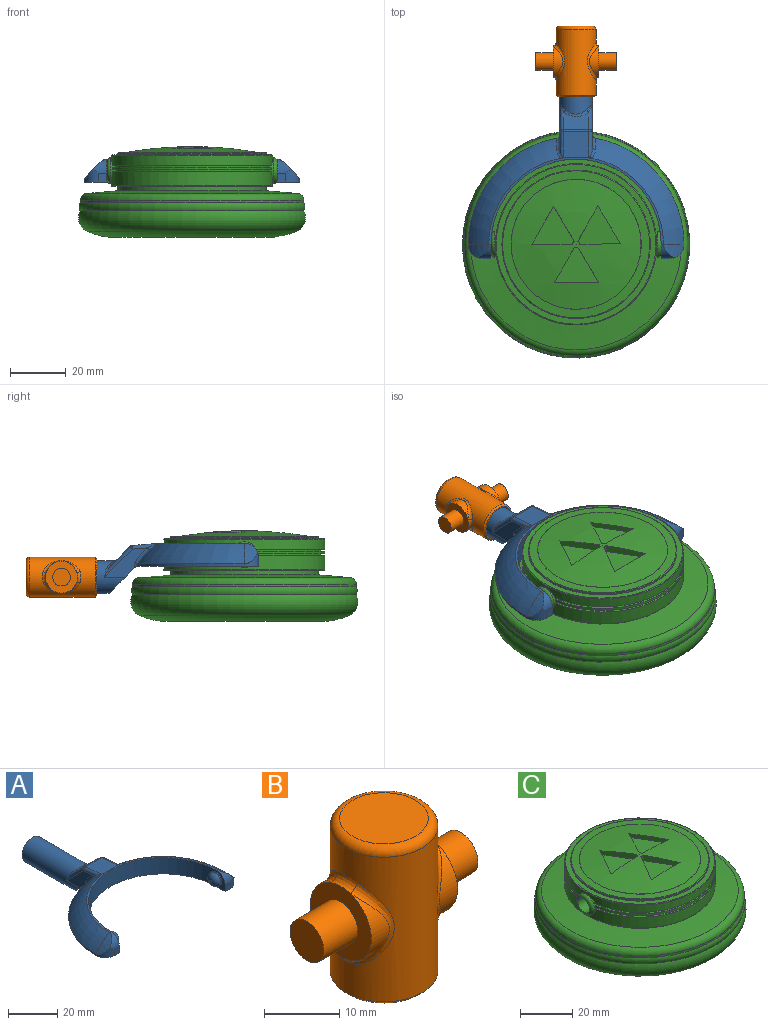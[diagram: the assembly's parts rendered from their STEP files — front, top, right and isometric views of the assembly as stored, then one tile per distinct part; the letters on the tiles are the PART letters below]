
ASSEMBLY  parts=3 mates=2
PART A: 48 faces, bbox 77.3x80.8x18.2 mm
  f0: plane 11.99x9.83mm, normal (0,-0.71,-0.71), area 141.5mm2, adj f1,f2,f9,f30,f43,f46
  f1: plane 15.39x10.49mm, normal (-1,0,0), area 63.5mm2, adj f0,f30,f32,f36,f46,f47
  f2: plane 15.39x10.49mm, normal (1,0,0), area 63.5mm2, adj f0,f30,f34,f39,f43,f44
  f3: plane 9.14x6.37mm, normal (0,0.71,0.71), area 67.6mm2, adj f35,f36,f39,f40
  f4: cylinder r=38.61mm len=37.99mm, axis (0,0,-1), area 42.6mm2, adj f6,f9,f17,f46,f47
  f5: torus R=19.3mm, axis (0,0,-1), area 507.8mm2, adj f10,f11,f12,f29,f42,f44
  f6: torus R=19.3mm, axis (0,0,-1), area 507.8mm2, adj f4,f11,f15,f28,f45,f47
  f7: cylinder r=30.48mm len=60.96mm, axis (0,0,-1), area 746.6mm2, adj f8,f9,f11,f14,f21,f24
  f8: plane 8.13x5.08mm, normal (-1,0,0), area 19.9mm2, adj f7,f9,f13,f19,f24
  f9: plane 77.22x43.73mm, normal (0,0,-1), area 956.2mm2, adj f0,f4,f7,f8,f10,f13,f14,f16
  f10: cylinder r=38.61mm len=37.99mm, axis (0,0,-1), area 42.6mm2, adj f5,f9,f20,f43,f44
  f11: plane 62.55x30.95mm, normal (0,0,1), area 75mm2, adj f5,f6,f7,f18,f19,f27
  f12: cylinder r=22.71mm len=7.33mm, axis (0,1,0), area 24.8mm2, adj f5,f19,f20
  f13: plane 3.05x3.05mm, normal (0,-1,0), area 9.3mm2, adj f8,f9,f19,f20
  f14: plane 8.13x5.08mm, normal (1,0,0), area 19.9mm2, adj f7,f9,f16,f18,f21
  f15: cylinder r=22.71mm len=7.33mm, axis (0,1,0), area 24.8mm2, adj f6,f17,f18
  f16: plane 3.05x3.05mm, normal (0,-1,0), area 9.3mm2, adj f9,f14,f17,f18
  f17: cylinder r=5.08mm len=5.08mm, axis (0,0,-1), area 21.9mm2, adj f4,f9,f15,f16,f18
  f18: cylinder r=5.08mm len=5.08mm, axis (-1,0,0), area 21.9mm2, adj f11,f14,f15,f16,f17
  f19: cylinder r=5.08mm len=5.08mm, axis (-1,0,0), area 21.9mm2, adj f8,f11,f12,f13,f20
  f20: cylinder r=5.08mm len=5.08mm, axis (0,0,-1), area 21.9mm2, adj f9,f10,f12,f13,f19
  f21: cylinder r=3.17mm len=6.35mm, axis (-1,0,0), area 12.7mm2, adj f7,f14,f23
  f22: plane 1.27x1.27mm, normal (1,0,0), area 1.3mm2, adj f23
  f23: torus R=0.64mm, axis (1,0,0), area 56.5mm2, adj f21,f22
  f24: cylinder r=3.17mm len=6.35mm, axis (1,0,0), area 12.7mm2, adj f7,f8,f26
  f25: plane 1.27x1.27mm, normal (-1,0,0), area 1.3mm2, adj f26
  f26: torus R=0.64mm, axis (-1,0,0), area 56.5mm2, adj f24,f25
  f27: plane 9.86x9.36mm, normal (0,0.09,1), area 85.6mm2, adj f11,f28,f29,f32,f34,f35,f42,f45
  f28: plane 1.04x0.17mm, normal (0,-1,0), area 0mm2, adj f6,f27,f45
  f29: plane 1.04x0.17mm, normal (0,-1,0), area 0mm2, adj f5,f27,f42
  f30: cylinder r=5.84mm len=33.01mm, axis (0,-1,0), area 1029.7mm2, adj f0,f1,f2,f31,f38,f40,f41
  f31: plane 11.68x11.68mm, normal (0,1,0), area 107.2mm2, adj f30
  f32: cylinder r=1.27mm len=9.13mm, axis (0,-1,0.09), area 14.4mm2, adj f1,f27,f33,f45
  f33: sphere r=1.27mm, area 1.5mm2, adj f32,f35,f36
  f34: cylinder r=1.27mm len=9.13mm, axis (0,1,-0.09), area 14.4mm2, adj f2,f27,f37,f42
  f35: cylinder r=1.27mm len=9.14mm, axis (-1,0,0), area 8.1mm2, adj f3,f27,f33,f37
  f36: cylinder r=1.27mm len=10.91mm, axis (0,-0.71,0.71), area 23.1mm2, adj f1,f3,f33,f38
  f37: sphere r=1.27mm, area 1.5mm2, adj f34,f35,f39
  f38: bspline ~4.55x2.75mm, area 2.3mm2, adj f30,f36,f40
  f39: cylinder r=1.27mm len=10.91mm, axis (0,0.71,-0.71), area 23.1mm2, adj f2,f3,f37,f41
  f40: bspline ~9.14x2.56mm, area 10.7mm2, adj f3,f30,f38,f41
  f41: bspline ~5.23x3.53mm, area 2.3mm2, adj f30,f39,f40
  f42: bspline ~4.62x3.14mm, area 5.2mm2, adj f5,f27,f29,f34,f44
  f43: cylinder r=1.27mm len=1.74mm, axis (0,0,-1), area 1.9mm2, adj f0,f2,f9,f10,f44
  f44: bspline ~8.6x7.86mm, area 11.9mm2, adj f2,f5,f10,f42,f43
  f45: bspline ~4.62x3.14mm, area 5.2mm2, adj f6,f27,f28,f32,f47
  f46: cylinder r=1.27mm len=1.74mm, axis (0,0,-1), area 1.9mm2, adj f0,f1,f4,f9,f47
  f47: bspline ~8.6x7.86mm, area 11.9mm2, adj f1,f4,f6,f45,f46
PART B: 25 faces, bbox 28.9x15.5x25.4 mm
  f0: cylinder r=5.71mm len=10.81mm, axis (-1,0,0), area 26.2mm2, adj f5,f15
  f1: cylinder r=5.71mm len=10.81mm, axis (-1,0,0), area 26.2mm2, adj f8,f11
  f2: cylinder r=7.14mm len=23.5mm, axis (0,0,-1), area 763.2mm2, adj f9,f10,f11,f12,f13,f14,f15,f16
  f3: plane 11.75x11.75mm, normal (0,0,1), area 108.4mm2, adj f17
  f4: plane 13.02x13.02mm, normal (0,0,-1), area 16.3mm2, adj f22,f24
  f5: plane 11.46x11.46mm, normal (1,0,0), area 70.9mm2, adj f0,f6,f13,f16,f18
  f6: cylinder r=5.71mm len=10.81mm, axis (-1,0,0), area 26.2mm2, adj f5,f14
  f7: cylinder r=5.71mm len=10.81mm, axis (-1,0,0), area 26.2mm2, adj f8,f10
  f8: plane 11.46x11.46mm, normal (-1,0,0), area 70.9mm2, adj f1,f7,f9,f12,f20
  f9: bspline ~4.64x1.73mm, area 6.5mm2, adj f2,f8,f10,f11
  f10: bspline ~13.62x4.91mm, area 20.7mm2, adj f2,f7,f9,f12
  f11: bspline ~13.6x4.87mm, area 20.7mm2, adj f1,f2,f9,f12
  f12: bspline ~4.64x1.73mm, area 6.5mm2, adj f2,f8,f10,f11
  f13: bspline ~4.64x1.73mm, area 6.5mm2, adj f2,f5,f14,f15
  f14: bspline ~13.62x4.91mm, area 20.7mm2, adj f2,f6,f13,f16
  f15: bspline ~13.6x4.87mm, area 20.7mm2, adj f0,f2,f13,f16
  f16: bspline ~4.64x1.73mm, area 6.5mm2, adj f2,f5,f14,f15
  f17: torus R=5.87mm, axis (0,0,1), area 83.8mm2, adj f2,f3
  f18: cylinder r=3.17mm len=6.35mm, axis (-1,0,0), area 126.7mm2, adj f5,f19
  f19: plane 6.35x6.35mm, normal (1,0,0), area 31.7mm2, adj f18
  f20: cylinder r=3.17mm len=6.35mm, axis (1,0,0), area 126.7mm2, adj f8,f21
  f21: plane 6.35x6.35mm, normal (-1,0,0), area 31.7mm2, adj f20
  f22: cylinder r=6.1mm len=22.86mm, axis (0,0,-1), area 875.6mm2, adj f4,f23
  f23: plane 12.19x12.19mm, normal (0,0,-1), area 116.7mm2, adj f22
  f24: cone r=7.14mm half-angle=45deg, axis (0,0,1), area 38.5mm2, adj f2,f4
PART C: 56 faces, bbox 96.2x96.2x32.5 mm
  f0: cylinder r=28.87mm len=57.73mm, axis (0,0,-1), area 855.6mm2, adj f5,f6,f46,f47,f52
  f1: plane 57.01x24.31mm, normal (0,0,-1), area 101mm2, adj f4,f7,f46,f47
  f2: plane 57.01x24.31mm, normal (0,0,-1), area 101mm2, adj f3,f8,f46,f47
  f3: cylinder r=27.6mm len=54.44mm, axis (0,0,1), area 49.2mm2, adj f2,f6,f46,f47
  f4: cylinder r=27.6mm len=54.44mm, axis (0,0,1), area 49.2mm2, adj f1,f5,f46,f47
  f5: plane 57.01x24.31mm, normal (0,0,1), area 101mm2, adj f0,f4,f46,f47
  f6: plane 57.01x24.31mm, normal (0,0,1), area 101mm2, adj f0,f3,f46,f47
  f7: cylinder r=28.87mm len=57.06mm, axis (0,0,-1), area 77.8mm2, adj f1,f13,f46,f47
  f8: cylinder r=28.87mm len=57.06mm, axis (0,0,-1), area 77.8mm2, adj f2,f14,f46,f47
  f9: plane 57.13x24.71mm, normal (0,0,-1), area 102mm2, adj f12,f15,f46,f47
  f10: plane 57.13x24.71mm, normal (0,0,-1), area 102mm2, adj f11,f15,f46,f47
  f11: cylinder r=27.6mm len=54.56mm, axis (0,0,1), area 49.6mm2, adj f10,f14,f46,f47
  f12: cylinder r=27.6mm len=54.56mm, axis (0,0,1), area 49.6mm2, adj f9,f13,f46,f47
  f13: plane 57.06x24.48mm, normal (0,0,1), area 101.4mm2, adj f7,f12,f46,f47
  f14: plane 57.06x24.48mm, normal (0,0,1), area 101.4mm2, adj f8,f11,f46,f47
  f15: cylinder r=28.87mm len=57.73mm, axis (0,0,-1), area 595.8mm2, adj f9,f10,f46,f47,f53
  f16: sphere r=135.39mm, area 1385.3mm2, adj f30,f31,f32,f33,f35,f36,f37,f38
  f17: plane 39.33x39.33mm, normal (0,0,-1), area 1214.6mm2, adj f18
  f18: torus R=20.12mm, axis (0,0,-1), area 1429.3mm2, adj f17,f19
  f19: torus R=27.74mm, axis (0,0,-1), area 3542.1mm2, adj f18,f20
  f20: torus R=35.36mm, axis (0,0,-1), area 2180.1mm2, adj f19,f21
  f21: torus R=37.35mm, axis (0,0,-1), area 734.6mm2, adj f20,f22
  f22: cylinder r=40.06mm len=80.11mm, axis (0,0,-1), area 213.3mm2, adj f21,f26
  f23: cone r=26.57mm half-angle=85deg, axis (0,0,-1), area 2265mm2, adj f24,f26
  f24: cylinder r=26.57mm len=53.14mm, axis (0,0,-1), area 265mm2, adj f23,f25
  f25: plane 57.23x57.23mm, normal (0,0,-1), area 354.5mm2, adj f24,f52
  f26: torus R=37.52mm, axis (0,0,1), area 928.6mm2, adj f22,f23
  f27: cone r=26.57mm half-angle=87deg, axis (0,0,-1), area 475.4mm2, adj f54,f55
  f28: cylinder r=26.57mm len=53.14mm, axis (0,0,-1), area 92.3mm2, adj f29,f54
  f29: plane 57.23x57.23mm, normal (0,0,1), area 354.5mm2, adj f28,f53
  f30: cylinder r=1.27mm len=2.53mm, axis (0,0,1), area 3.4mm2, adj f16,f31,f33,f34
  f31: plane 12.57x7.44mm, normal (-0.86,-0.51,0), area 32.2mm2, adj f16,f30,f32,f34
  f32: plane 13.84x7.78mm, normal (0.87,-0.49,0), area 28mm2, adj f16,f31,f33,f34
  f33: plane 14.6x2.53mm, normal (-0.01,1,0), area 32.2mm2, adj f16,f30,f32,f34
  f34: plane 15.23x13.84mm, normal (0,0,1), area 108.3mm2, adj f30,f31,f32,f33
  f35: cylinder r=1.27mm len=2.53mm, axis (0,0,1), area 3.4mm2, adj f16,f36,f38,f39
  f36: plane 14.6x2.53mm, normal (-0.01,1,0), area 32.2mm2, adj f16,f35,f37,f39
  f37: plane 13.66x8.09mm, normal (-0.86,-0.51,0), area 28mm2, adj f16,f36,f38,f39
  f38: plane 12.73x7.16mm, normal (0.87,-0.49,0), area 32.2mm2, adj f16,f35,f37,f39
  f39: plane 15.25x13.82mm, normal (0,0,1), area 108.3mm2, adj f35,f36,f37,f38
  f40: cylinder r=1.27mm len=2.53mm, axis (0,0,1), area 3.4mm2, adj f16,f41,f43,f44
  f41: plane 12.73x7.16mm, normal (0.87,-0.49,0), area 32.2mm2, adj f16,f40,f42,f44
  f42: plane 15.87x1.84mm, normal (-0.01,1,0), area 28mm2, adj f16,f41,f43,f44
  f43: plane 12.57x7.44mm, normal (-0.86,-0.51,0), area 32.2mm2, adj f16,f40,f42,f44
  f44: plane 15.87x12.74mm, normal (0,0,1), area 108.3mm2, adj f40,f41,f42,f43
  f45: plane 6.6x6.6mm, normal (1,0,0), area 2.6mm2, adj f50,f51
  f46: cylinder r=4.57mm len=9.14mm, axis (-1,0,0), area 18.4mm2, adj f0,f1,f2,f3,f4,f5,f6,f7
  f47: cylinder r=4.57mm len=9.14mm, axis (-1,0,0), area 18.4mm2, adj f0,f1,f2,f3,f4,f5,f6,f7
  f48: plane 6.6x6.6mm, normal (-1,0,0), area 2.6mm2, adj f49,f51
  f49: torus R=3.3mm, axis (1,0,0), area 51.5mm2, adj f47,f48
  f50: torus R=3.3mm, axis (1,0,0), area 51.5mm2, adj f45,f46
  f51: cylinder r=3.17mm len=60.96mm, axis (1,0,0), area 1216.1mm2, adj f45,f48
  f52: torus R=28.61mm, axis (0,0,1), area 72.1mm2, adj f0,f25
  f53: torus R=28.61mm, axis (0,0,-1), area 72.1mm2, adj f15,f29
  f54: torus R=26.31mm, axis (0,0,1), area 64.2mm2, adj f27,f28
  f55: torus R=23.29mm, axis (0,0,1), area 4.5mm2, adj f16,f27
PLACE A t=(32.34,27.52,20.85)mm
PLACE B rot(axis=(-1,0,0),90deg) t=(32.34,80.3,16.88)mm
PLACE C t=(32.34,27.52,33.52)mm
MATE revolute A.f24 <-> C.f46  axis (-1,0,0) through (62.82,27.52,24.92)mm
MATE revolute B.f2 <-> A.f30  axis (0,-1,0) through (32.34,103.16,16.88)mm
